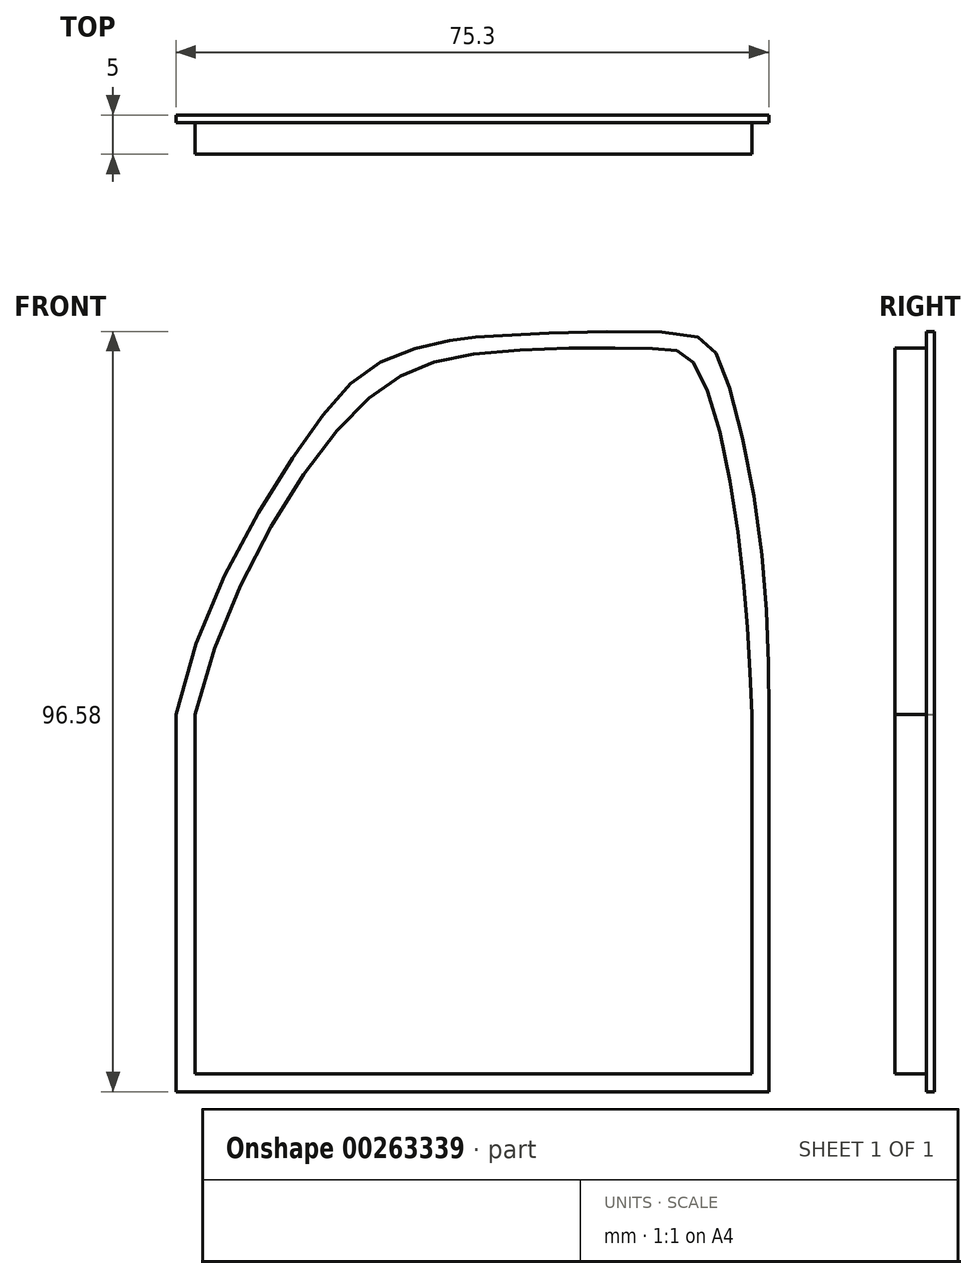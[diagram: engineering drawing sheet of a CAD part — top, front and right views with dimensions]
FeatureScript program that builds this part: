
annotation { "Feature Type Name" : "Feature", "Feature Type Description" : "" }
export const myFeature = defineFeature(function(context is Context, id is Id, definition is map)
    precondition{}
    {
        {
            var Q0;
            Q0=qCreatedBy(makeId("Front.planeOp"),FACE);
            var sketch = newSketch(context, id + "F0", { "sketchPlane" : qUnion([Q0])});
            skLineSegment(sketch, "E0.bottom", {"start": v(-6.38, 46.5) * mm, "end": v(21.95, 46.5) * mm});
            skLineSegment(sketch, "E0.top", {"start": v(-46.59, -55.14) * mm, "end": v(33.83, -55.14) * mm});
            skLineSegment(sketch, "E0.left", {"start": v(-46.59, -4.32) * mm, "end": v(-46.59, -55.14) * mm});
            skLineSegment(sketch, "E0.right", {"start": v(33.83, 19.6) * mm, "end": v(33.83, -55.14) * mm});
            skFitSpline(sketch, "E1", {"points": [v(-46.59, -4.32) * mm, v(-30.87, 31) * mm, v(-20.25, 41.13) * mm, v(-6.38, 46.5) * mm], "startDerivative": vector(17.33, 88.44) * mm, "endDerivative": vector(60.56, 8.43) * mm});
            skPoint(sketch, "E2.orphan", {"position": v(-46.59, 46.5) * mm});
            skFitSpline(sketch, "E3", {"points": [v(21.95, 46.5) * mm, v(27.63, 41.64) * mm, v(33.83, 19.6) * mm, v(33.83, 3.49) * mm, v(33.83, 3.37) * mm], "startDerivative": vector(25.35, -15.2) * mm, "endDerivative": vector(0.18, -3.1) * mm});
            skPoint(sketch, "E4.orphan", {"position": v(33.83, 46.5) * mm});
            skLineSegment(sketch, "E5.top", {"start": v(-43.68, -52.26) * mm, "end": v(31.62, -52.26) * mm});
            skLineSegment(sketch, "E5.left", {"start": v(-43.68, -4.32) * mm, "end": v(-43.68, -52.26) * mm});
            skLineSegment(sketch, "E5.right", {"start": v(31.62, -4.32) * mm, "end": v(31.62, -52.26) * mm});
            skFitSpline(sketch, "E6", {"points": [v(-43.68, -4.32) * mm, v(-27, 31) * mm, v(-17.27, 40.65) * mm, v(-7.5, 43.38) * mm, v(-1.6, 43.84) * mm, v(20.74, 44) * mm, v(25.12, 41.13) * mm, v(30.28, 19.6) * mm, v(31.62, -4.32) * mm], "startDerivative": vector(40.76, 206.76) * mm, "endDerivative": vector(0.55, -146.46) * mm});
            skLineSegment(sketch, "E7.top", {"start": v(-41.28, -50.03) * mm, "end": v(29.47, -50.03) * mm});
            skLineSegment(sketch, "E7.left", {"start": v(-41.28, -4.32) * mm, "end": v(-41.28, -50.03) * mm});
            skLineSegment(sketch, "E7.right", {"start": v(29.47, -4.32) * mm, "end": v(29.47, -50.03) * mm});
            skFitSpline(sketch, "E8", {"points": [v(29.47, -4.32) * mm, v(27.6, 19.6) * mm, v(21.96, 40.45) * mm, v(16.9, 42.14) * mm, v(-5.95, 41.4) * mm, v(-20.95, 34.2) * mm, v(-41.28, -4.32) * mm], "startDerivative": vector(-5.83, 122.07) * mm, "endDerivative": vector(-47.07, -192.85) * mm});
            skSolve(sketch);
        }
        {
            var Q0;
            Q0=makeQuery(id+"F0.imprint","IMPRINT",FACE,{"disambiguationData":[TD([[makeQuery(id+"F0.imprint","IMPRINT",EDGE,{"derivedFrom":sQuery(id+"F0.wireOp",EDGE,"E5.top")}),1.0]])]});
            extrude(context, id + "F1", {"entities" : qUnion([Q0]), "depth" : 1 * mm});
        }
        {
            var Q0;
            Q0=makeQuery(id+"F0.imprint","IMPRINT",FACE,{"disambiguationData":[TD([[makeQuery(id+"F0.imprint","IMPRINT",EDGE,{"derivedFrom":sQuery(id+"F0.wireOp",EDGE,"E7.top")}),1.0]])]});
            extrude(context, id + "F2", {"entities" : qUnion([Q0]), "operationType" : NewBodyOperationType.ADD, "depth" : 5 * mm});
        }
    });
